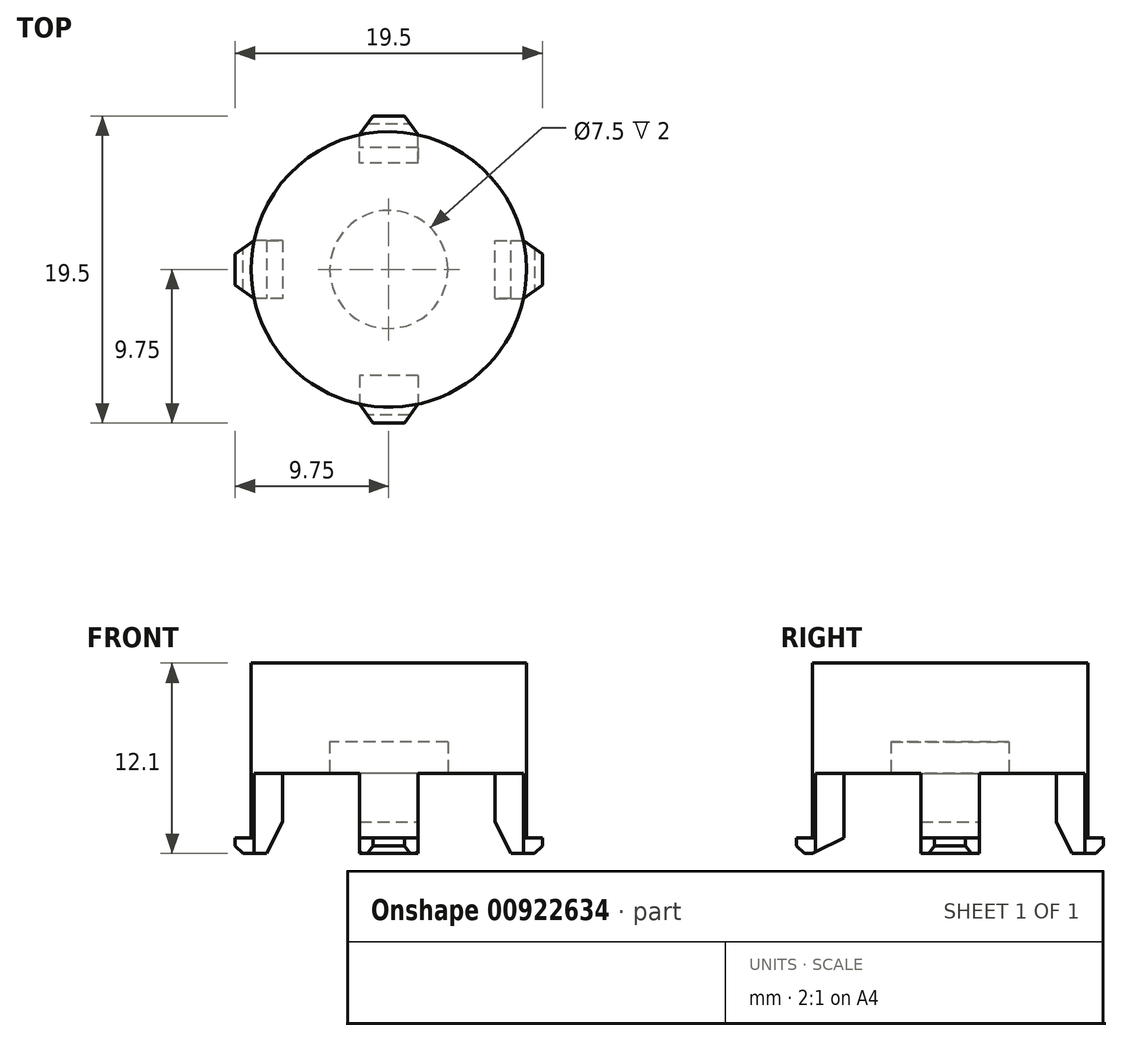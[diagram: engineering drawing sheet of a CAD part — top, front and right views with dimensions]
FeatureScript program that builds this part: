
annotation { "Feature Type Name" : "Feature", "Feature Type Description" : "" }
export const myFeature = defineFeature(function(context is Context, id is Id, definition is map)
    precondition{}
    {
        {
            var Q0;
            Q0=qCreatedBy(makeId("Top.planeOp"),FACE);
            var sketch = newSketch(context, id + "F0", { "sketchPlane" : qUnion([Q0])});
            skCircle(sketch, "E0", {"center": v(0, 0) * mm, "radius": 8.75 * mm});
            skCircle(sketch, "E1", {"center": v(0, 0) * mm, "radius": 3.75 * mm});
            skLineSegment(sketch, "E2", {"start": v(0, 6.75) * mm, "end": v(-1.85, 6.75) * mm});
            skLineSegment(sketch, "E3", {"start": v(-1.85, 6.75) * mm, "end": v(-1.85, 8.55) * mm});
            skLineSegment(sketch, "E4.MirrorCS", {"start": v(0, 6.75) * mm, "end": v(1.85, 6.75) * mm});
            skLineSegment(sketch, "E5.MirrorCS", {"start": v(1.85, 6.75) * mm, "end": v(1.85, 8.55) * mm});
            skLineSegment(sketch, "E6.1.0", {"start": v(-6.75, -1.85) * mm, "end": v(-8.55, -1.85) * mm});
            skLineSegment(sketch, "E6.1.1", {"start": v(-6.75, 0) * mm, "end": v(-6.75, -1.85) * mm});
            skLineSegment(sketch, "E6.1.2", {"start": v(-6.75, 0) * mm, "end": v(-6.75, 1.85) * mm});
            skLineSegment(sketch, "E6.1.3", {"start": v(-6.75, 1.85) * mm, "end": v(-8.55, 1.85) * mm});
            skLineSegment(sketch, "E6.2.0", {"start": v(1.85, -6.75) * mm, "end": v(1.85, -8.55) * mm});
            skLineSegment(sketch, "E6.2.1", {"start": v(0, -6.75) * mm, "end": v(1.85, -6.75) * mm});
            skLineSegment(sketch, "E6.2.2", {"start": v(0, -6.75) * mm, "end": v(-1.85, -6.75) * mm});
            skLineSegment(sketch, "E6.2.3", {"start": v(-1.85, -6.75) * mm, "end": v(-1.85, -8.55) * mm});
            skLineSegment(sketch, "E6.3.0", {"start": v(6.75, 1.85) * mm, "end": v(8.55, 1.85) * mm});
            skLineSegment(sketch, "E6.3.1", {"start": v(6.75, 0) * mm, "end": v(6.75, 1.85) * mm});
            skLineSegment(sketch, "E6.3.2", {"start": v(6.75, 0) * mm, "end": v(6.75, -1.85) * mm});
            skLineSegment(sketch, "E6.3.3", {"start": v(6.75, -1.85) * mm, "end": v(8.55, -1.85) * mm});
            skSolve(sketch);
        }
        {
            var Q0;
            Q0=makeQuery(id+"F0.imprint","IMPRINT",FACE,{"disambiguationData":[TD([[makeQuery(id+"F0.imprint","IMPRINT",EDGE,{"derivedFrom":sQuery(id+"F0.wireOp",EDGE,"E1")}),-1.0]])]});
            var Q1;
            {var subQ0=sQuery(id+"F0.wireOp",EDGE,"E6.1.0");Q1=makeQuery(id+"F0.imprint","IMPRINT",FACE,{"disambiguationData":[TD([[makeQuery(id+"F0.imprint","IMPRINT",EDGE,{"derivedFrom":subQ0}),-1.0]])]});}
            var Q2;
            Q2=makeQuery(id+"F0.imprint","IMPRINT",FACE,{"disambiguationData":[TD([[makeQuery(id+"F0.imprint","IMPRINT",EDGE,{"derivedFrom":sQuery(id+"F0.wireOp",EDGE,"E2")}),-1.0]])]});
            var Q3;
            {var subQ0=sQuery(id+"F0.wireOp",EDGE,"E6.3.0");Q3=makeQuery(id+"F0.imprint","IMPRINT",FACE,{"disambiguationData":[TD([[makeQuery(id+"F0.imprint","IMPRINT",EDGE,{"derivedFrom":subQ0}),-1.0]])]});}
            var Q4;
            {var subQ0=sQuery(id+"F0.wireOp",EDGE,"E6.2.0");Q4=makeQuery(id+"F0.imprint","IMPRINT",FACE,{"disambiguationData":[TD([[makeQuery(id+"F0.imprint","IMPRINT",EDGE,{"derivedFrom":subQ0}),-1.0]])]});}
            var Q5;
            Q5=makeQuery(id+"F0.imprint","IMPRINT",FACE,{"disambiguationData":[TD([[makeQuery(id+"F0.imprint","IMPRINT",EDGE,{"derivedFrom":sQuery(id+"F0.wireOp",EDGE,"E1")}),1.0]])]});
            extrude(context, id + "F1", {"entities" : qUnion([Q0, Q1, Q2, Q3, Q4, Q5]), "depth" : 7 * mm, "offsetDistance" : 25 * mm});
        }
        {
            var Q0;
            {var subQ0=sQuery(id+"F0.wireOp",EDGE,"E6.1.0");Q0=makeQuery(id+"F0.imprint","IMPRINT",FACE,{"disambiguationData":[TD([[makeQuery(id+"F0.imprint","IMPRINT",EDGE,{"derivedFrom":subQ0}),-1.0]])]});}
            var Q1;
            {var subQ0=sQuery(id+"F0.wireOp",EDGE,"E6.2.0");Q1=makeQuery(id+"F0.imprint","IMPRINT",FACE,{"disambiguationData":[TD([[makeQuery(id+"F0.imprint","IMPRINT",EDGE,{"derivedFrom":subQ0}),-1.0]])]});}
            var Q2;
            {var subQ0=sQuery(id+"F0.wireOp",EDGE,"E6.3.0");Q2=makeQuery(id+"F0.imprint","IMPRINT",FACE,{"disambiguationData":[TD([[makeQuery(id+"F0.imprint","IMPRINT",EDGE,{"derivedFrom":subQ0}),-1.0]])]});}
            var Q3;
            Q3=makeQuery(id+"F0.imprint","IMPRINT",FACE,{"disambiguationData":[TD([[makeQuery(id+"F0.imprint","IMPRINT",EDGE,{"derivedFrom":sQuery(id+"F0.wireOp",EDGE,"E2")}),-1.0]])]});
            extrude(context, id + "F2", {"entities" : qUnion([Q0, Q1, Q2, Q3]), "operationType" : NewBodyOperationType.ADD, "oppositeDirection" : true, "depth" : 3.1 * mm + 2 * mm, "offsetDistance" : 25 * mm});
        }
        {
            var Q0;
            Q0=makeQuery(id+"F0.imprint","IMPRINT",FACE,{"disambiguationData":[TD([[makeQuery(id+"F0.imprint","IMPRINT",EDGE,{"derivedFrom":sQuery(id+"F0.wireOp",EDGE,"E1")}),1.0]])]});
            extrude(context, id + "F3", {"entities" : qUnion([Q0]), "operationType" : NewBodyOperationType.REMOVE, "depth" : 2 * mm, "offsetDistance" : 25 * mm});
        }
        {
            var Q0;
            Q0=makeQuery(id+"F2.opExtrude","CAP_FACE",FACE,{"disambiguationData":[OSD([sQuery(id+"F0.wireOp",EDGE,"E0"),sQuery(id+"F0.wireOp",EDGE,"E2"),sQuery(id+"F0.wireOp",EDGE,"E3"),sQuery(id+"F0.wireOp",EDGE,"E4.MirrorCS"),sQuery(id+"F0.wireOp",EDGE,"E5.MirrorCS")])],"isStart":false});
            var sketch = newSketch(context, id + "F4", { "sketchPlane" : qUnion([Q0])});
            skCircle(sketch, "E7.0", {"center": v(0, 0) * mm, "radius": 8.75 * mm});
            skLineSegment(sketch, "E8", {"start": v(0.99, -9.75) * mm, "end": v(-0.99, -9.75) * mm});
            skPoint(sketch, "E9.center", {"position": v(-0.39, 0.39) * mm});
            skLineSegment(sketch, "E10", {"start": v(1.85, -8.55) * mm, "end": v(0.99, -9.75) * mm});
            skLineSegment(sketch, "E11.MirrorCS", {"start": v(-1.85, -8.55) * mm, "end": v(-0.99, -9.75) * mm});
            skPoint(sketch, "E12.orphan", {"position": v(-1.85, -9.75) * mm});
            skLineSegment(sketch, "E13.1.0", {"start": v(8.55, 1.85) * mm, "end": v(9.75, 0.99) * mm});
            skLineSegment(sketch, "E13.1.1", {"start": v(9.75, 0.99) * mm, "end": v(9.75, -0.99) * mm});
            skLineSegment(sketch, "E13.1.2", {"start": v(8.55, -1.85) * mm, "end": v(9.75, -0.99) * mm});
            skLineSegment(sketch, "E13.2.0", {"start": v(-1.85, 8.55) * mm, "end": v(-0.99, 9.75) * mm});
            skLineSegment(sketch, "E13.2.1", {"start": v(-0.99, 9.75) * mm, "end": v(0.99, 9.75) * mm});
            skLineSegment(sketch, "E13.2.2", {"start": v(1.85, 8.55) * mm, "end": v(0.99, 9.75) * mm});
            skLineSegment(sketch, "E13.3.0", {"start": v(-8.55, -1.85) * mm, "end": v(-9.75, -0.99) * mm});
            skLineSegment(sketch, "E13.3.1", {"start": v(-9.75, -0.99) * mm, "end": v(-9.75, 0.99) * mm});
            skLineSegment(sketch, "E13.3.2", {"start": v(-8.55, 1.85) * mm, "end": v(-9.75, 0.99) * mm});
            skSolve(sketch);
        }
        {
            var Q0;
            {var subQ2=sQuery(id+"F4.wireOp",EDGE,"9MO0csZw-w4PH-vTgd-ioZy-cVQajA3temSK");Q0=makeQuery(id+"F4.imprint","IMPRINT",FACE,{"disambiguationData":[TD([[makeQuery(id+"F4.imprint","IMPRINT",EDGE,{"derivedFrom":subQ2}),-1.0]])]});}
            var Q1;
            {var subQ0=sQuery(id+"F4.wireOp",EDGE,"E9.2.0");Q1=makeQuery(id+"F4.imprint","IMPRINT",FACE,{"disambiguationData":[TD([[makeQuery(id+"F4.imprint","IMPRINT",EDGE,{"derivedFrom":subQ0}),-1.0]])]});}
            var Q2;
            {var subQ0=sQuery(id+"F4.wireOp",EDGE,"E9.1.0");Q2=makeQuery(id+"F4.imprint","IMPRINT",FACE,{"disambiguationData":[TD([[makeQuery(id+"F4.imprint","IMPRINT",EDGE,{"derivedFrom":subQ0}),-1.0]])]});}
            var Q3;
            {var subQ0=sQuery(id+"F4.wireOp",EDGE,"E9.3.0");Q3=makeQuery(id+"F4.imprint","IMPRINT",FACE,{"disambiguationData":[TD([[makeQuery(id+"F4.imprint","IMPRINT",EDGE,{"derivedFrom":subQ0}),-1.0]])]});}
            var Q4;
            {var subQ1=makeQuery(id+"F2.opExtrude","CAP_EDGE",EDGE,{"disambiguationData":[OSD([sQuery(id+"F0.wireOp",EDGE,"E3")])],"isStart":false});Q4=makeQuery(id+"F4.imprint","IMPRINT",FACE,{"disambiguationData":[TD([[makeQuery(id+"F4.imprint","IMPRINT",EDGE,{"derivedFrom":subQ1}),1.0]])]});}
            extrude(context, id + "F5", {"entities" : qUnion([Q0, Q1, Q2, Q3, Q4]), "operationType" : NewBodyOperationType.ADD, "oppositeDirection" : true, "depth" : 1 * mm, "offsetDistance" : 25 * mm});
        }
        {
            var Q0;
            Q0=makeQuery(id+"F4.imprint","IMPRINT",FACE,{"disambiguationData":[TD([[makeQuery(id+"F4.imprint","IMPRINT",EDGE,{"derivedFrom":sQuery(id+"F4.wireOp",EDGE,"E8")}),-1.0]])]});
            var Q1;
            {var subQ0=sQuery(id+"F4.wireOp",EDGE,"E13.1.0");Q1=makeQuery(id+"F4.imprint","IMPRINT",FACE,{"disambiguationData":[TD([[makeQuery(id+"F4.imprint","IMPRINT",EDGE,{"derivedFrom":subQ0}),-1.0]])]});}
            var Q2;
            {var subQ0=sQuery(id+"F4.wireOp",EDGE,"E13.2.0");Q2=makeQuery(id+"F4.imprint","IMPRINT",FACE,{"disambiguationData":[TD([[makeQuery(id+"F4.imprint","IMPRINT",EDGE,{"derivedFrom":subQ0}),-1.0]])]});}
            var Q3;
            {var subQ0=sQuery(id+"F4.wireOp",EDGE,"E13.3.0");Q3=makeQuery(id+"F4.imprint","IMPRINT",FACE,{"disambiguationData":[TD([[makeQuery(id+"F4.imprint","IMPRINT",EDGE,{"derivedFrom":subQ0}),-1.0]])]});}
            extrude(context, id + "F6", {"entities" : qUnion([Q0, Q1, Q2, Q3]), "operationType" : NewBodyOperationType.ADD, "oppositeDirection" : true, "depth" : 1 * mm, "offsetDistance" : 25 * mm});
        }
        {
            var Q0;
            Q0=makeQuery(id+"F6.opExtrude","CAP_EDGE",EDGE,{"disambiguationData":[OSD([sQuery(id+"F4.wireOp",EDGE,"E8")])],"isStart":true});
            var Q1;
            Q1=makeQuery(id+"F6.opExtrude","CAP_EDGE",EDGE,{"disambiguationData":[OSD([sQuery(id+"F4.wireOp",EDGE,"E13.1.1")])],"isStart":true});
            var Q2;
            Q2=makeQuery(id+"F6.opExtrude","CAP_EDGE",EDGE,{"disambiguationData":[OSD([sQuery(id+"F4.wireOp",EDGE,"E13.2.1")])],"isStart":true});
            var Q3;
            Q3=makeQuery(id+"F6.opExtrude","CAP_EDGE",EDGE,{"disambiguationData":[OSD([sQuery(id+"F4.wireOp",EDGE,"E13.3.1")])],"isStart":true});
            chamfer(context, id + "F7", {"entities" : qUnion([Q0, Q1, Q2, Q3]), "width" : 0.5 * mm, "tangentPropagation" : true});
        }
        {
            var Q0;
            Q0=makeQuery(id+"F2.opExtrude","CAP_EDGE",EDGE,{"disambiguationData":[OSD([sQuery(id+"F0.wireOp",EDGE,"E6.3.1"),sQuery(id+"F0.wireOp",EDGE,"E6.3.2")])],"isStart":false});
            var Q1;
            Q1=makeQuery(id+"F2.opExtrude","CAP_EDGE",EDGE,{"disambiguationData":[OSD([sQuery(id+"F0.wireOp",EDGE,"E2"),sQuery(id+"F0.wireOp",EDGE,"E4.MirrorCS")])],"isStart":false});
            var Q2;
            Q2=makeQuery(id+"F2.opExtrude","CAP_EDGE",EDGE,{"disambiguationData":[OSD([sQuery(id+"F0.wireOp",EDGE,"E6.1.1"),sQuery(id+"F0.wireOp",EDGE,"E6.1.2")])],"isStart":false});
            var Q3;
            Q3=makeQuery(id+"F2.opExtrude","CAP_EDGE",EDGE,{"disambiguationData":[OSD([sQuery(id+"F0.wireOp",EDGE,"E6.2.1"),sQuery(id+"F0.wireOp",EDGE,"E6.2.2")])],"isStart":false});
            chamfer(context, id + "F8", {"entities" : qUnion([Q0, Q1, Q2, Q3]), "chamferType" : ChamferType.TWO_OFFSETS, "width1" : 1 * mm, "oppositeDirection" : false, "width2" : 2 * mm, "tangentPropagation" : true});
        }
    });
